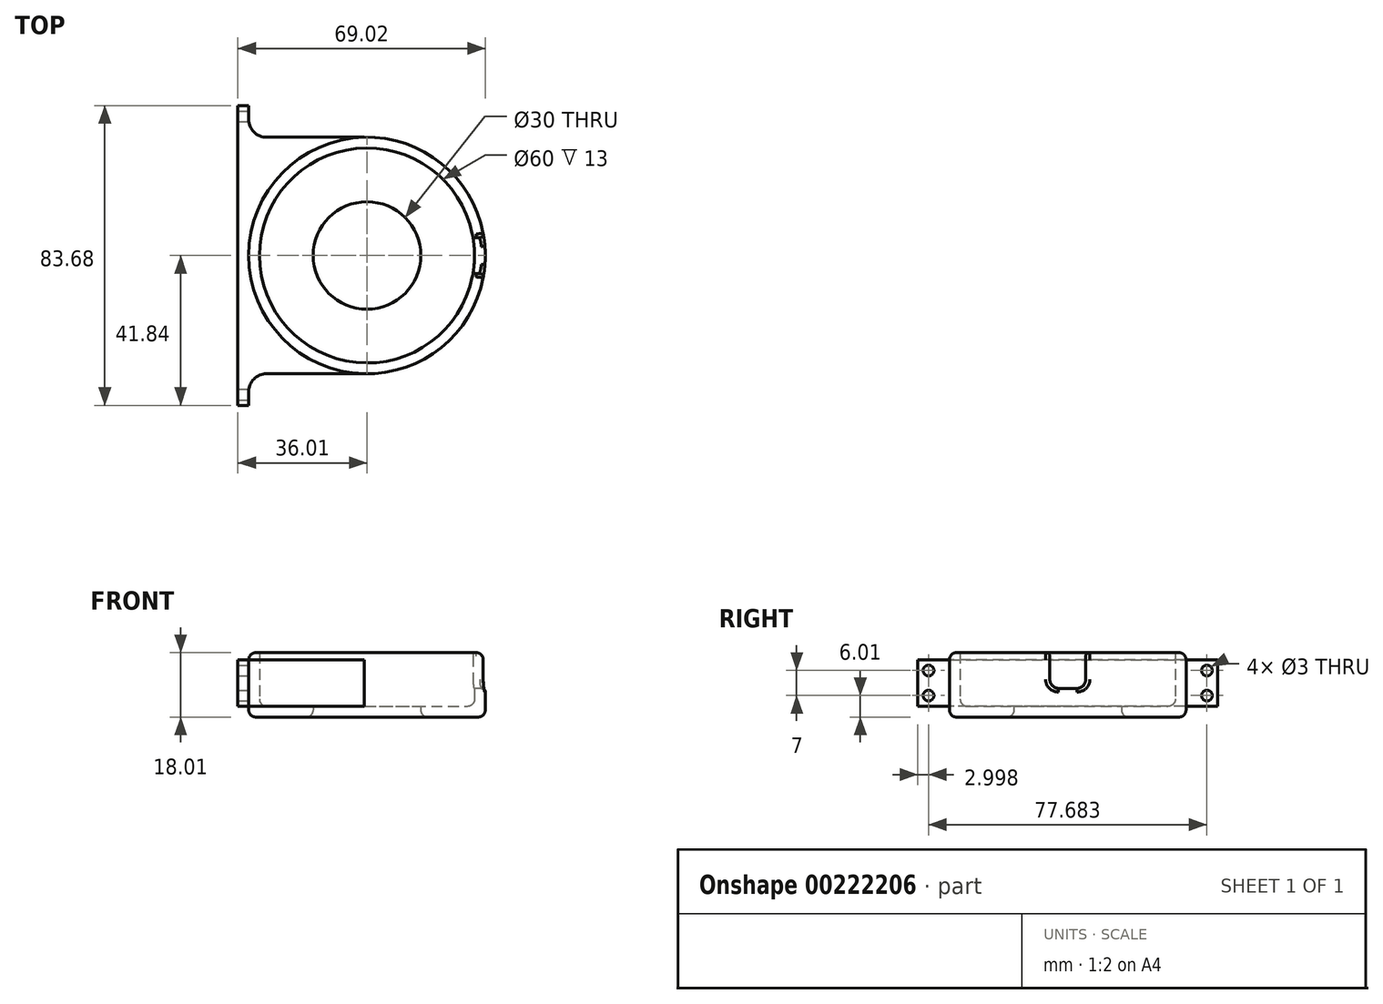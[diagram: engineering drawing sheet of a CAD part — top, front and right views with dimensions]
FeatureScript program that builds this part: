
annotation { "Feature Type Name" : "Feature", "Feature Type Description" : "" }
export const myFeature = defineFeature(function(context is Context, id is Id, definition is map)
    precondition{}
    {
        {
            var Q0;
            Q0=qCreatedBy(makeId("Front.planeOp"),FACE);
            var sketch = newSketch(context, id + "F0", { "sketchPlane" : qUnion([Q0])});
            skLineSegment(sketch, "E0", {"start": v(0, 0) * mm, "end": v(0, 30.68) * mm});
            skLineSegment(sketch, "E1", {"start": v(-15, 0) * mm, "end": v(-28, 0) * mm});
            skLineSegment(sketch, "E2", {"start": v(-30, 2) * mm, "end": v(-30, 15) * mm});
            skLineSegment(sketch, "E3.0", {"start": v(-33, -1.01) * mm, "end": v(-33, 13) * mm});
            skLineSegment(sketch, "E3.1", {"start": v(-17, -3) * mm, "end": v(-31, -3.01) * mm});
            skLineSegment(sketch, "E4", {"start": v(-31, 15) * mm, "end": v(-30, 15) * mm});
            skLineSegment(sketch, "E5", {"start": v(-15, 0) * mm, "end": v(-15, -1) * mm});
            skPoint(sketch, "E6.visualSharp", {"position": v(-33, -3.01) * mm});
            skArc(sketch, "E6.filletArc", {"start": v(-33, -1.01) * mm, "mid": v(-32.42, -2.42) * mm, "end": v(-31, -3.01) * mm});
            skPoint(sketch, "E7.visualSharp", {"position": v(-30, 0) * mm});
            skArc(sketch, "E7.filletArc", {"start": v(-30, 2) * mm, "mid": v(-29.41, 0.59) * mm, "end": v(-28, 0) * mm});
            skPoint(sketch, "E8.visualSharp", {"position": v(-15, -3) * mm});
            skArc(sketch, "E8.filletArc", {"start": v(-17, -3) * mm, "mid": v(-15.59, -2.42) * mm, "end": v(-15, -1) * mm});
            skPoint(sketch, "E9.visualSharp", {"position": v(-33, 15) * mm});
            skArc(sketch, "E9.filletArc", {"start": v(-31, 15) * mm, "mid": v(-32.42, 14.41) * mm, "end": v(-33, 13) * mm});
            skSolve(sketch);
        }
        {
            var Q0;
            Q0=makeQuery(id+"F0.imprint","IMPRINT",FACE,{"disambiguationData":[TD([[makeQuery(id+"F0.imprint","IMPRINT",EDGE,{"derivedFrom":sQuery(id+"F0.wireOp",EDGE,"E1")}),1.0]])]});
            var Q1;
            Q1=sQuery(id+"F0.wireOp",EDGE,"E0");
            revolve(context, id + "F1", {"entities" : qUnion([Q0]), "axis" : qUnion([Q1]), "revolveType" : RevolveType.FULL});
        }
        {
            var Q0;
            Q0=qCreatedBy(makeId("Top.planeOp"),FACE);
            var sketch = newSketch(context, id + "F2", { "sketchPlane" : qUnion([Q0])});
            skLineSegment(sketch, "E10", {"start": v(-33, 0) * mm, "end": v(-36, 0) * mm});
            skLineSegment(sketch, "E11", {"start": v(0, 33) * mm, "end": v(-28.01, 33) * mm});
            skLineSegment(sketch, "E12", {"start": v(-33.01, 38) * mm, "end": v(-33.01, 41.84) * mm});
            skLineSegment(sketch, "E13", {"start": v(-33.01, 41.84) * mm, "end": v(-36.01, 41.84) * mm});
            skLineSegment(sketch, "E14", {"start": v(-36.01, 41.84) * mm, "end": v(-36, 0) * mm});
            skPoint(sketch, "E15.visualSharp", {"position": v(-33.01, 33) * mm});
            skArc(sketch, "E15.filletArc", {"start": v(-33.01, 38) * mm, "mid": v(-31.55, 34.46) * mm, "end": v(-28.01, 33) * mm});
            skPoint(sketch, "E16", {"position": v(-34.5, 39.84) * mm});
            skLineSegment(sketch, "E17.MirrorCS", {"start": v(-33.01, -38) * mm, "end": v(-33.01, -41.84) * mm});
            skLineSegment(sketch, "E18.MirrorCS", {"start": v(-33, -41.84) * mm, "end": v(-36, -41.84) * mm});
            skArc(sketch, "E19.MirrorCS", {"start": v(-33, -38) * mm, "mid": v(-31.55, -34.46) * mm, "end": v(-28, -33) * mm});
            skPoint(sketch, "E20.MirrorP", {"position": v(-33.01, -33) * mm});
            skLineSegment(sketch, "E21.MirrorCS", {"start": v(-36, -41.84) * mm, "end": v(-36, 0) * mm});
            skLineSegment(sketch, "E22.MirrorCS", {"start": v(0, -33) * mm, "end": v(-28, -33) * mm});
            skPoint(sketch, "E23.MirrorP", {"position": v(-34.5, -39.84) * mm});
            skArc(sketch, "E24", {"start": v(0, 33) * mm, "mid": v(-33, 0) * mm, "end": v(0, -33) * mm});
            skSolve(sketch);
        }
        {
            var Q0;
            {var subQ1=sQuery(id+"F2.wireOp",EDGE,"E10");Q0=makeQuery(id+"F2.imprint","IMPRINT",FACE,{"disambiguationData":[TD([[makeQuery(id+"F2.imprint","IMPRINT",EDGE,{"derivedFrom":subQ1}),-1.0]])]});}
            var Q1;
            {var subQ0=sQuery(id+"F2.wireOp",EDGE,"E10");Q1=makeQuery(id+"F2.imprint","IMPRINT",FACE,{"disambiguationData":[TD([[makeQuery(id+"F2.imprint","IMPRINT",EDGE,{"derivedFrom":subQ0}),1.0]])]});}
            extrude(context, id + "F3", {"entities" : qUnion([Q0, Q1]), "operationType" : NewBodyOperationType.ADD, "depth" : 13 * mm});
        }
        {
            var Q0;
            Q0=qCreatedBy(makeId("Right.planeOp"),FACE);
            cPlane(context, id + "F4", {"entities" : qUnion([Q0]), "cplaneType" : CPlaneType.OFFSET, "offset" : 30 * mm, "oppositeDirection" : true, "width" : 150 * mm, "height" : 150 * mm});
        }
        {
            var Q0;
            Q0=qCreatedBy(id+"F4.planeOp",FACE);
            var sketch = newSketch(context, id + "F5", { "sketchPlane" : qUnion([Q0])});
            skPoint(sketch, "E25", {"position": v(38.84, 10) * mm});
            skPoint(sketch, "E26", {"position": v(38.84, 3) * mm});
            skPoint(sketch, "E27.MirrorP", {"position": v(-38.84, 3) * mm});
            skPoint(sketch, "E28.MirrorP", {"position": v(-38.84, 10) * mm});
            skSolve(sketch);
        }
        {
            var Q0;
            Q0=sQuery(id+"F5.wireOp",VERTEX,"E28.MirrorP");
            var Q1;
            Q1=sQuery(id+"F5.wireOp",VERTEX,"E27.MirrorP");
            var Q2;
            Q2=sQuery(id+"F5.wireOp",VERTEX,"E26");
            var Q3;
            Q3=sQuery(id+"F5.wireOp",VERTEX,"E25");
            var Q4;
            Q4=makeQuery(id+"F1.opRevolve","SWEPT_BODY",BODY,{"disambiguationData":[OSD([sQuery(id+"F0.wireOp",EDGE,"E1"),sQuery(id+"F0.wireOp",EDGE,"E2"),sQuery(id+"F0.wireOp",EDGE,"E3.0"),sQuery(id+"F0.wireOp",EDGE,"E3.1"),sQuery(id+"F0.wireOp",EDGE,"E4"),sQuery(id+"F0.wireOp",EDGE,"E5"),sQuery(id+"F0.wireOp",EDGE,"E6.filletArc"),sQuery(id+"F0.wireOp",EDGE,"E7.filletArc"),sQuery(id+"F0.wireOp",EDGE,"E8.filletArc"),sQuery(id+"F0.wireOp",EDGE,"E9.filletArc")])]});
            hole(context, id + "F6", {"style" : HoleStyle.SIMPLE, "endStyle" : HoleEndStyle.THROUGH, "holeDiameter" : 3 * mm, "startFromSketch" : true, "locations" : qUnion([Q0, Q1, Q2, Q3]), "scope" : qUnion([Q4]), "isTappedThrough" : true});
        }
        {
            var Q0;
            Q0=qCreatedBy(makeId("Right.planeOp"),FACE);
            var sketch = newSketch(context, id + "F7", { "sketchPlane" : qUnion([Q0])});
            skLineSegment(sketch, "E29", {"start": v(-5, 15) * mm, "end": v(5, 15) * mm});
            skLineSegment(sketch, "E30", {"start": v(5, 15) * mm, "end": v(5, 7.5) * mm});
            skLineSegment(sketch, "E31", {"start": v(2.5, 5) * mm, "end": v(-2.5, 5) * mm});
            skLineSegment(sketch, "E32", {"start": v(-5, 7.5) * mm, "end": v(-5, 15) * mm});
            skPoint(sketch, "E33.visualSharp", {"position": v(-5, 5) * mm});
            skArc(sketch, "E33.filletArc", {"start": v(-5, 7.5) * mm, "mid": v(-4.27, 5.73) * mm, "end": v(-2.5, 5) * mm});
            skPoint(sketch, "E34.visualSharp", {"position": v(5, 5) * mm});
            skArc(sketch, "E34.filletArc", {"start": v(2.5, 5) * mm, "mid": v(4.27, 5.73) * mm, "end": v(5, 7.5) * mm});
            skSolve(sketch);
        }
        {
            var Q0;
            Q0 = qSketchRegion(id + "F7", true);
            extrude(context, id + "F8", {"entities" : qUnion([Q0]), "operationType" : NewBodyOperationType.REMOVE, "depth" : 68 * mm});
        }
        {
            var Q0;
            Q0=makeQuery(id+"F8.boolean.opBoolean","INTERSECT",EDGE,{"derivedFrom":[makeQuery(id+"F1.opRevolve","SWEPT_FACE",FACE,{"disambiguationData":[OSD([sQuery(id+"F0.wireOp",EDGE,"E3.0")])]}),makeQuery(id+"F8.opExtrude","SWEPT_FACE",FACE,{"disambiguationData":[OSD([sQuery(id+"F7.wireOp",EDGE,"E33.filletArc")])]})]});
            var Q1;
            Q1=makeQuery(id+"F8.boolean.opBoolean","INTERSECT",EDGE,{"derivedFrom":[makeQuery(id+"F1.opRevolve","SWEPT_FACE",FACE,{"disambiguationData":[OSD([sQuery(id+"F0.wireOp",EDGE,"E3.0")])]}),makeQuery(id+"F8.opExtrude","SWEPT_FACE",FACE,{"disambiguationData":[OSD([sQuery(id+"F7.wireOp",EDGE,"E31")])]})]});
            var Q2;
            Q2=makeQuery(id+"F8.boolean.opBoolean","INTERSECT",EDGE,{"derivedFrom":[makeQuery(id+"F1.opRevolve","SWEPT_FACE",FACE,{"disambiguationData":[OSD([sQuery(id+"F0.wireOp",EDGE,"E3.0")])]}),makeQuery(id+"F8.opExtrude","SWEPT_FACE",FACE,{"disambiguationData":[OSD([sQuery(id+"F7.wireOp",EDGE,"E34.filletArc")])]})]});
            var Q3;
            Q3=makeQuery(id+"F8.boolean.opBoolean","INTERSECT",EDGE,{"derivedFrom":[makeQuery(id+"F1.opRevolve","SWEPT_FACE",FACE,{"disambiguationData":[OSD([sQuery(id+"F0.wireOp",EDGE,"E3.0")])]}),makeQuery(id+"F8.opExtrude","SWEPT_FACE",FACE,{"disambiguationData":[OSD([sQuery(id+"F7.wireOp",EDGE,"E30")])]})]});
            var Q4;
            Q4=makeQuery(id+"F8.boolean.opBoolean","INTERSECT",EDGE,{"derivedFrom":[makeQuery(id+"F1.opRevolve","SWEPT_FACE",FACE,{"disambiguationData":[OSD([sQuery(id+"F0.wireOp",EDGE,"E3.0")])]}),makeQuery(id+"F8.opExtrude","SWEPT_FACE",FACE,{"disambiguationData":[OSD([sQuery(id+"F7.wireOp",EDGE,"E32")])]})]});
            fillet(context, id + "F9", {"entities" : qUnion([Q0, Q1, Q2, Q3, Q4]), "radius" : 1 * mm, "tangentPropagation" : true, "allowEdgeOverflow" : false});
        }
    });
